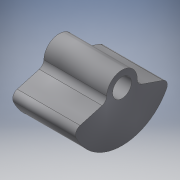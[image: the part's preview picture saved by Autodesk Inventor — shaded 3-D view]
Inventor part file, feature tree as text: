
AUTODESK INVENTOR PART (.ipt)
format: ipt  version: 2016 (Build 200138000, 138)  size: 146,944 bytes
history: native  units: in
note: dims shown in document units (in); Inventor stores cm internally (conversion verified against a paired STEP export)
features: extrude x1, sketch x1
ambient origin geometry x8: Origin, YZ Plane, XZ Plane, XY Plane, X Axis, Y Axis, Z Axis, Center Point
bodies: Solid1 (feature_tree)
feature tree (2):
  extrude  "Extrusion1"  Depth=0.0787in TaperAngle=0.0deg
  sketch  "Sketch1"  dims[d3=0.0236in d4=0.0787in d5=0.0in d10=0.0079in]
